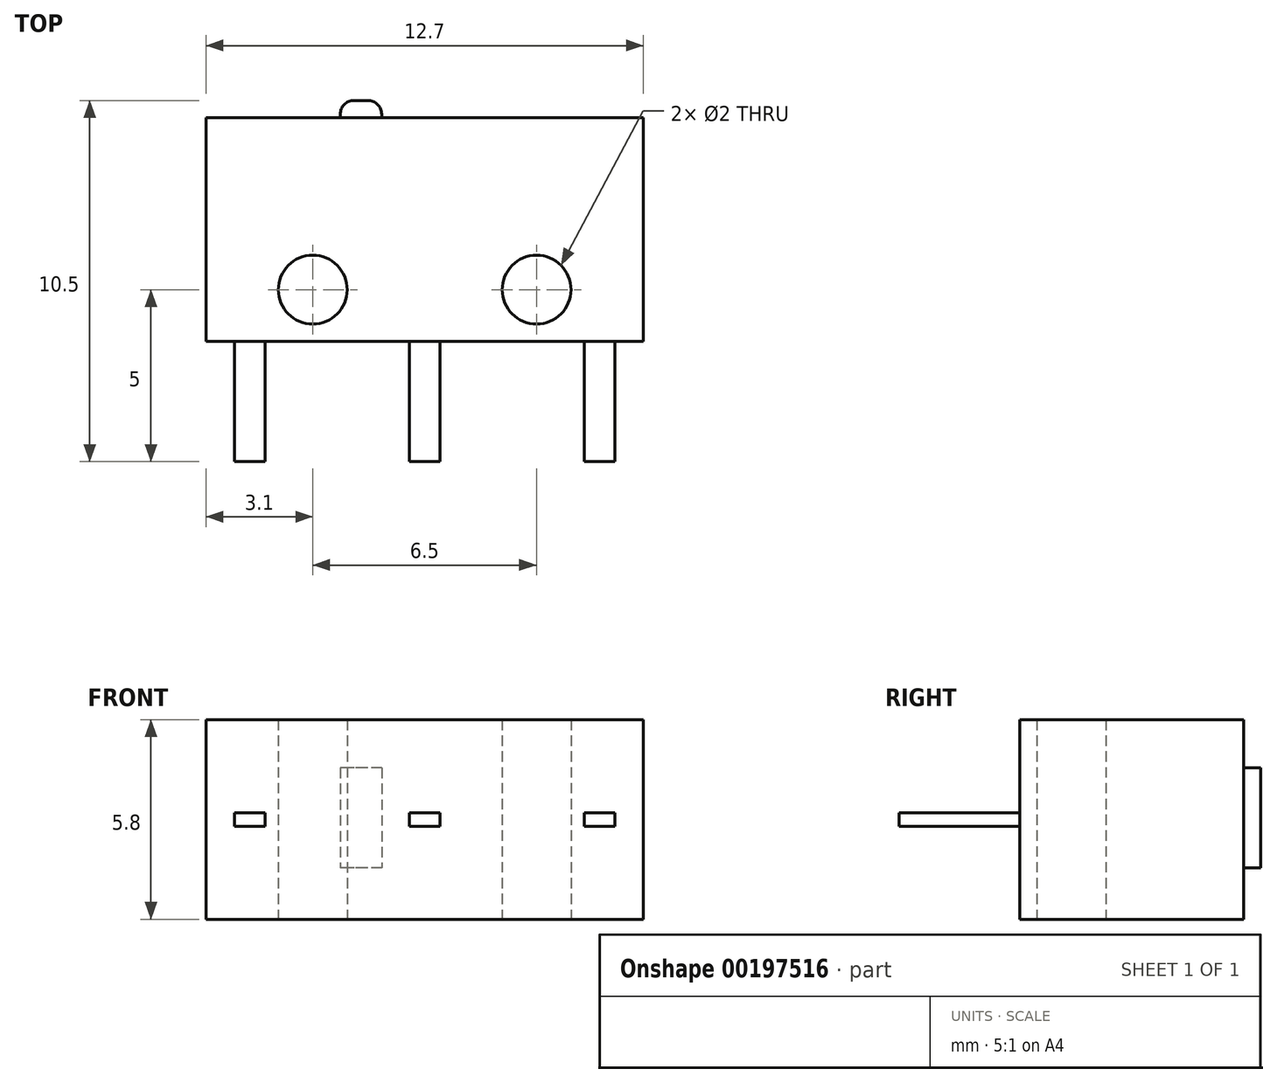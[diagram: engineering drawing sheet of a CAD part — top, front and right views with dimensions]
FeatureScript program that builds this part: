
annotation { "Feature Type Name" : "Feature", "Feature Type Description" : "" }
export const myFeature = defineFeature(function(context is Context, id is Id, definition is map)
    precondition{}
    {
        {
            var Q0;
            Q0=qCreatedBy(makeId("Top.planeOp"),FACE);
            var sketch = newSketch(context, id + "F0", { "sketchPlane" : qUnion([Q0])});
            skLineSegment(sketch, "E0.bottom", {"start": v(-6.35, 3.25) * mm, "end": v(6.35, 3.25) * mm});
            skLineSegment(sketch, "E0.top", {"start": v(-6.35, -3.25) * mm, "end": v(6.35, -3.25) * mm});
            skLineSegment(sketch, "E0.left", {"start": v(-6.35, 3.25) * mm, "end": v(-6.35, -3.25) * mm});
            skLineSegment(sketch, "E0.right", {"start": v(6.35, 3.25) * mm, "end": v(6.35, -3.25) * mm});
            skCircle(sketch, "E1", {"center": v(-3.25, -1.75) * mm, "radius": 1 * mm});
            skCircle(sketch, "E2", {"center": v(3.25, -1.75) * mm, "radius": 1 * mm});
            skSolve(sketch);
        }
        {
            var Q0;
            Q0=qSketchRegion(id+"F0",true);
            extrude(context, id + "F1", {"entities" : qUnion([Q0]), "depth" : 5.8 * mm});
        }
        {
            var Q0;
            Q0=makeQuery(id+"F1.opExtrude","SWEPT_FACE",FACE,{"disambiguationData":[OSD([sQuery(id+"F0.wireOp",EDGE,"E0.bottom")])]});
            var sketch = newSketch(context, id + "F2", { "sketchPlane" : qUnion([Q0])});
            skLineSegment(sketch, "E3.bottom", {"start": v(1.25, 4.4) * mm, "end": v(2.45, 4.4) * mm});
            skLineSegment(sketch, "E3.top", {"start": v(1.25, 1.5) * mm, "end": v(2.45, 1.5) * mm});
            skLineSegment(sketch, "E3.left", {"start": v(1.25, 4.4) * mm, "end": v(1.25, 1.5) * mm});
            skLineSegment(sketch, "E3.right", {"start": v(2.45, 4.4) * mm, "end": v(2.45, 1.5) * mm});
            skLineSegment(sketch, "E4", {"start": v(-3.15, 5.8) * mm, "end": v(-3.15, 0) * mm, "construction": true});
            skSolve(sketch);
        }
        {
            var Q0;
            Q0=qCreatedBy(makeId("Top.planeOp"),FACE);
            cPlane(context, id + "F3", {"entities" : qUnion([Q0]), "cplaneType" : CPlaneType.OFFSET, "offset" : 2.7 * mm, "width" : 150 * mm, "height" : 150 * mm});
        }
        {
            var Q0;
            Q0=qCreatedBy(id+"F3.planeOp",FACE);
            var sketch = newSketch(context, id + "F4", { "sketchPlane" : qUnion([Q0])});
            skLineSegment(sketch, "E5.bottom", {"start": v(-5.53, -3.25) * mm, "end": v(-4.63, -3.25) * mm});
            skLineSegment(sketch, "E5.top", {"start": v(-5.53, -6.75) * mm, "end": v(-4.63, -6.75) * mm});
            skLineSegment(sketch, "E5.left", {"start": v(-5.53, -3.25) * mm, "end": v(-5.53, -6.75) * mm});
            skLineSegment(sketch, "E5.right", {"start": v(-4.63, -3.25) * mm, "end": v(-4.63, -6.75) * mm});
            skLineSegment(sketch, "E6.bottom", {"start": v(-0.45, -3.25) * mm, "end": v(0.45, -3.25) * mm});
            skLineSegment(sketch, "E6.top", {"start": v(-0.45, -6.75) * mm, "end": v(0.45, -6.75) * mm});
            skLineSegment(sketch, "E6.left", {"start": v(-0.45, -3.25) * mm, "end": v(-0.45, -6.75) * mm});
            skLineSegment(sketch, "E6.right", {"start": v(0.45, -3.25) * mm, "end": v(0.45, -6.75) * mm});
            skLineSegment(sketch, "E7.bottom", {"start": v(4.63, -3.25) * mm, "end": v(5.53, -3.25) * mm});
            skLineSegment(sketch, "E7.top", {"start": v(4.63, -6.75) * mm, "end": v(5.53, -6.75) * mm});
            skLineSegment(sketch, "E7.left", {"start": v(4.63, -3.25) * mm, "end": v(4.63, -6.75) * mm});
            skLineSegment(sketch, "E7.right", {"start": v(5.53, -3.25) * mm, "end": v(5.53, -6.75) * mm});
            skSolve(sketch);
        }
        {
            var Q0;
            Q0=qSketchRegion(id+"F4",true);
            extrude(context, id + "F5", {"entities" : qUnion([Q0]), "operationType" : NewBodyOperationType.ADD, "depth" : 0.4 * mm});
        }
        {
            var Q0;
            Q0=qSketchRegion(id+"F2",true);
            extrude(context, id + "F6", {"entities" : qUnion([Q0]), "operationType" : NewBodyOperationType.ADD, "depth" : .5 * mm});
        }
        {
            var Q0;
            Q0=makeQuery(id+"F6.opExtrude","CAP_EDGE",EDGE,{"disambiguationData":[OSD([sQuery(id+"F2.wireOp",EDGE,"E3.right")])],"isStart":false});
            var Q1;
            Q1=makeQuery(id+"F6.opExtrude","CAP_EDGE",EDGE,{"disambiguationData":[OSD([sQuery(id+"F2.wireOp",EDGE,"E3.left")])],"isStart":false});
            fillet(context, id + "F7", {"entities" : qUnion([Q0, Q1]), "radius" : .4 * mm, "tangentPropagation" : true, "allowEdgeOverflow" : false});
        }
    });
